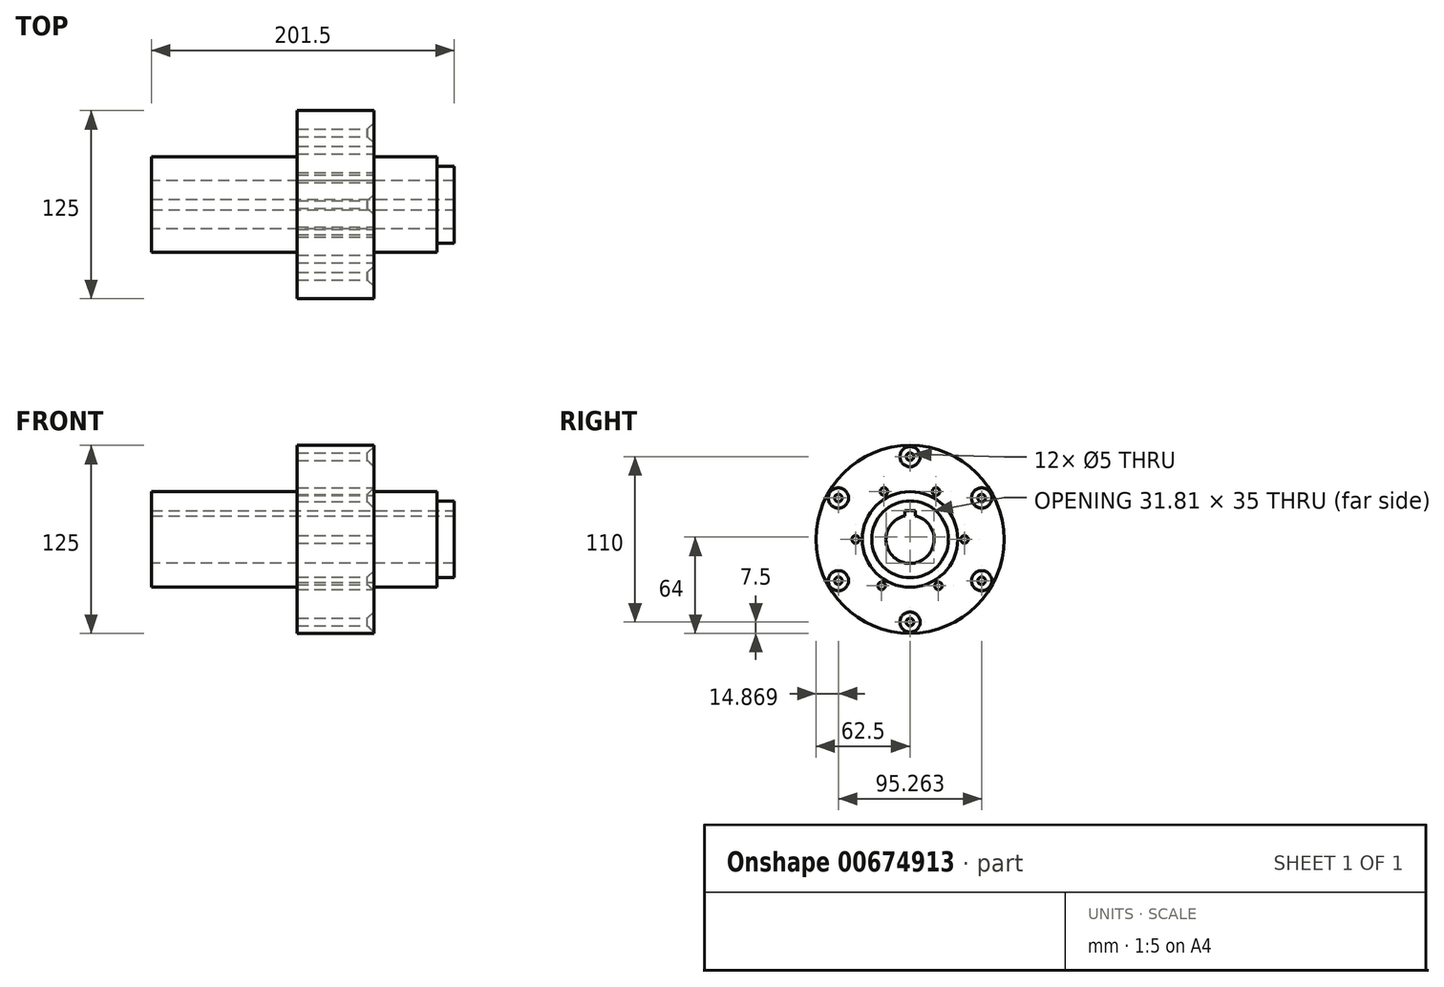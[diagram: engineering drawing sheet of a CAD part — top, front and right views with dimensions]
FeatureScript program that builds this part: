
annotation { "Feature Type Name" : "Feature", "Feature Type Description" : "" }
export const myFeature = defineFeature(function(context is Context, id is Id, definition is map)
    precondition{}
    {
        {
            var Q0;
            Q0=qCreatedBy(makeId("Front.planeOp"),FACE);
            var sketch = newSketch(context, id + "F0", { "sketchPlane" : qUnion([Q0])});
            skLineSegment(sketch, "E0", {"start": v(-294.45, 0) * mm, "end": v(331.76, 0) * mm, "construction": true});
            skLineSegment(sketch, "E1", {"start": v(-272.3, 16) * mm, "end": v(-70.8, 16) * mm});
            skLineSegment(sketch, "E2", {"start": v(-70.8, 16) * mm, "end": v(-70.8, 25.5) * mm});
            skLineSegment(sketch, "E3", {"start": v(-70.8, 25.5) * mm, "end": v(-82.3, 25.5) * mm});
            skLineSegment(sketch, "E4", {"start": v(-82.3, 25.5) * mm, "end": v(-82.3, 31.75) * mm});
            skLineSegment(sketch, "E5", {"start": v(-82.3, 31.75) * mm, "end": v(-149.3, 31.75) * mm});
            skLineSegment(sketch, "E6", {"start": v(-149.3, 31.75) * mm, "end": v(-149.3, 62.5) * mm});
            skLineSegment(sketch, "E7", {"start": v(-149.3, 62.5) * mm, "end": v(-175.3, 62.5) * mm});
            skLineSegment(sketch, "E8", {"start": v(-175.3, 62.5) * mm, "end": v(-175.3, 31.75) * mm});
            skLineSegment(sketch, "E9", {"start": v(-175.3, 31.75) * mm, "end": v(-272.3, 31.75) * mm});
            skLineSegment(sketch, "E10", {"start": v(-272.3, 31.75) * mm, "end": v(-272.3, 16) * mm});
            skSolve(sketch);
        }
        {
            var Q0;
            Q0=makeQuery(id+"F0.imprint","IMPRINT",FACE,{"disambiguationData":[TD([[makeQuery(id+"F0.imprint","IMPRINT",EDGE,{"derivedFrom":sQuery(id+"F0.wireOp",EDGE,"E1")}),1.0]])]});
            var Q1;
            Q1=sQuery(id+"F0.wireOp",EDGE,"E0");
            revolve(context, id + "F1", {"entities" : qUnion([Q0]), "axis" : qUnion([Q1]), "revolveType" : RevolveType.FULL});
        }
        {
            var Q0;
            Q0=makeQuery(id+"F1.opRevolve","SWEPT_FACE",FACE,{"disambiguationData":[OSD([sQuery(id+"F0.wireOp",EDGE,"E6")])]});
            extrude(context, id + "F2", {"entities" : qUnion([Q0]), "operationType" : NewBodyOperationType.ADD, "depth" : 25 * mm, "offsetDistance" : 25 * mm});
        }
        {
            var Q0;
            Q0=makeQuery(id+"F2.opExtrude","CAP_FACE",FACE,{"disambiguationData":[OSD([sQuery(id+"F0.wireOp",EDGE,"E6")])],"isStart":false});
            var sketch = newSketch(context, id + "F3", { "sketchPlane" : qUnion([Q0])});
            skCircle(sketch, "E11", {"center": v(0, 0) * mm, "radius": 55 * mm, "construction": true});
            skPoint(sketch, "E12", {"position": v(0, 55) * mm});
            skPoint(sketch, "E13", {"position": v(47.63, 27.5) * mm});
            skPoint(sketch, "E14", {"position": v(47.63, -27.5) * mm});
            skPoint(sketch, "E15", {"position": v(0, -55) * mm});
            skPoint(sketch, "E16", {"position": v(-47.63, -27.5) * mm});
            skPoint(sketch, "E17", {"position": v(-47.63, 27.5) * mm});
            skLineSegment(sketch, "E18", {"start": v(0, 91.53) * mm, "end": v(0, -99.55) * mm, "construction": true});
            skLineSegment(sketch, "E19", {"start": v(-87.53, 0) * mm, "end": v(116.48, 0) * mm, "construction": true});
            skLineSegment(sketch, "E20", {"start": v(-89.5, 51.67) * mm, "end": v(89.5, -51.67) * mm, "construction": true});
            skLineSegment(sketch, "E21", {"start": v(-69.32, -40.02) * mm, "end": v(69.32, 40.02) * mm, "construction": true});
            skSolve(sketch);
        }
        {
            var Q0;
            Q0=sQuery(id+"F3.wireOp",VERTEX,"E17");
            var Q1;
            Q1=sQuery(id+"F3.wireOp",VERTEX,"E13");
            var Q2;
            Q2=sQuery(id+"F3.wireOp",VERTEX,"E12");
            var Q3;
            Q3=sQuery(id+"F3.wireOp",VERTEX,"E15");
            var Q4;
            Q4=sQuery(id+"F3.wireOp",VERTEX,"E14");
            var Q5;
            Q5=sQuery(id+"F3.wireOp",VERTEX,"E16");
            var Q6;
            Q6=makeQuery(id+"F1.opRevolve","SWEPT_BODY",BODY,{"disambiguationData":[OSD([sQuery(id+"F0.wireOp",EDGE,"E1"),sQuery(id+"F0.wireOp",EDGE,"E2"),sQuery(id+"F0.wireOp",EDGE,"E3"),sQuery(id+"F0.wireOp",EDGE,"E4"),sQuery(id+"F0.wireOp",EDGE,"E5"),sQuery(id+"F0.wireOp",EDGE,"E6"),sQuery(id+"F0.wireOp",EDGE,"E7"),sQuery(id+"F0.wireOp",EDGE,"E8"),sQuery(id+"F0.wireOp",EDGE,"E9"),sQuery(id+"F0.wireOp",EDGE,"E10")])]});
            hole(context, id + "F4", {"style" : HoleStyle.C_SINK, "endStyle" : HoleEndStyle.THROUGH, "standardTappedOrClearance" : lookupTablePath({ "standard" : "ISO", "engagement" : "75%", "pitch" : "1 mm", "size" : "M6", "type" : "Tapped" }), "standardBlindInLast" : lookupTablePath({ "standard" : "ISO", "engagement" : "75%", "pitch" : "1 mm", "size" : "M6", "type" : "Tapped" }), "holeDiameter" : 5 * mm, "cSinkDiameter" : 13.44 * mm, "cSinkAngle" : 90 * degree, "majorDiameter" : 6 * mm, "showTappedDepth" : true, "isTappedThrough" : true, "tappedDepth" : 16.25 * mm, "tapClearance" : 3, "locations" : qUnion([Q0, Q1, Q2, Q3, Q4, Q5]), "scope" : qUnion([Q6])});
        }
        {
            var Q0;
            Q0=makeQuery(id+"F2.opExtrude","CAP_FACE",FACE,{"disambiguationData":[OSD([sQuery(id+"F0.wireOp",EDGE,"E6")])],"isStart":false});
            var sketch = newSketch(context, id + "F5", { "sketchPlane" : qUnion([Q0])});
            skCircle(sketch, "E22", {"center": v(0, 0) * mm, "radius": 36.2 * mm, "construction": true});
            skLineSegment(sketch, "E23", {"start": v(38.45, 68.39) * mm, "end": v(-52.12, -88.5) * mm, "construction": true});
            skLineSegment(sketch, "E24", {"start": v(-44.25, 78.43) * mm, "end": v(65.92, -112.4) * mm, "construction": true});
            skLineSegment(sketch, "E25", {"start": v(-94.96, 0) * mm, "end": v(138.2, 0) * mm, "construction": true});
            skPoint(sketch, "E26", {"position": v(17.32, 31.79) * mm});
            skPoint(sketch, "E27", {"position": v(36.2, 0) * mm});
            skPoint(sketch, "E28", {"position": v(18.87, -30.9) * mm});
            skPoint(sketch, "E29", {"position": v(-18.87, -30.9) * mm});
            skPoint(sketch, "E30", {"position": v(-36.2, 0) * mm});
            skPoint(sketch, "E31", {"position": v(-17.32, 31.79) * mm});
            skSolve(sketch);
        }
        {
            var Q0;
            Q0=sQuery(id+"F5.wireOp",VERTEX,"E30");
            var Q1;
            Q1=sQuery(id+"F5.wireOp",VERTEX,"E31");
            var Q2;
            Q2=sQuery(id+"F5.wireOp",VERTEX,"E26");
            var Q3;
            Q3=sQuery(id+"F5.wireOp",VERTEX,"E27");
            var Q4;
            Q4=sQuery(id+"F5.wireOp",VERTEX,"E28");
            var Q5;
            Q5=sQuery(id+"F5.wireOp",VERTEX,"E29");
            var Q6;
            Q6=makeQuery(id+"F1.opRevolve","SWEPT_BODY",BODY,{"disambiguationData":[OSD([sQuery(id+"F0.wireOp",EDGE,"E1"),sQuery(id+"F0.wireOp",EDGE,"E2"),sQuery(id+"F0.wireOp",EDGE,"E3"),sQuery(id+"F0.wireOp",EDGE,"E4"),sQuery(id+"F0.wireOp",EDGE,"E5"),sQuery(id+"F0.wireOp",EDGE,"E6"),sQuery(id+"F0.wireOp",EDGE,"E7"),sQuery(id+"F0.wireOp",EDGE,"E8"),sQuery(id+"F0.wireOp",EDGE,"E9"),sQuery(id+"F0.wireOp",EDGE,"E10")])]});
            hole(context, id + "F6", {"style" : HoleStyle.SIMPLE, "endStyle" : HoleEndStyle.THROUGH, "standardTappedOrClearance" : lookupTablePath({ "standard" : "ISO", "engagement" : "75%", "pitch" : "1 mm", "size" : "M6", "type" : "Tapped" }), "standardBlindInLast" : lookupTablePath({ "standard" : "ISO", "engagement" : "75%", "pitch" : "1 mm", "size" : "M6", "type" : "Tapped" }), "holeDiameter" : 5 * mm, "majorDiameter" : 6 * mm, "showTappedDepth" : true, "isTappedThrough" : true, "tappedDepth" : 16.25 * mm, "tapClearance" : 3, "locations" : qUnion([Q0, Q1, Q2, Q3, Q4, Q5]), "scope" : qUnion([Q6])});
        }
        {
            var Q0;
            Q0=makeQuery(id+"F1.opRevolve","SWEPT_FACE",FACE,{"disambiguationData":[OSD([sQuery(id+"F0.wireOp",EDGE,"E2")])]});
            var sketch = newSketch(context, id + "F7", { "sketchPlane" : qUnion([Q0])});
            skLineSegment(sketch, "E32.bottom", {"start": v(3.5, 13) * mm, "end": v(-3.5, 13) * mm});
            skLineSegment(sketch, "E32.top", {"start": v(3.5, 19) * mm, "end": v(-3.5, 19) * mm});
            skLineSegment(sketch, "E32.left", {"start": v(3.5, 13) * mm, "end": v(3.5, 19) * mm});
            skLineSegment(sketch, "E32.right", {"start": v(-3.5, 13) * mm, "end": v(-3.5, 19) * mm});
            skPoint(sketch, "E32.middle", {"position": v(0, 16) * mm});
            skSolve(sketch);
        }
        {
            var Q0;
            {var subQ0=sQuery(id+"F7.wireOp",EDGE,"E32.top");Q0=makeQuery(id+"F7.imprint","IMPRINT",FACE,{"disambiguationData":[TD([[makeQuery(id+"F7.imprint","IMPRINT",EDGE,{"derivedFrom":subQ0}),1.0]])]});}
            extrude(context, id + "F8", {"entities" : qUnion([Q0]), "operationType" : NewBodyOperationType.REMOVE, "endBound" : BoundingType.UP_TO_NEXT, "oppositeDirection" : true, "depth" : 25 * mm, "offsetDistance" : 25 * mm});
        }
    });
